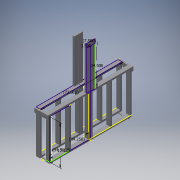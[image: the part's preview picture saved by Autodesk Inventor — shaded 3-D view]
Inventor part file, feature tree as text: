
AUTODESK INVENTOR PART (.ipt)
format: ipt  version: 2019 (Build 230136000, 136)  size: 350,720 bytes
history: native  units: in
note: dims shown in document units (in); Inventor stores cm internally (conversion verified against a paired STEP export)
features: sketch x19, extrude x8
ambient origin geometry x8: Origin, YZ Plane, XZ Plane, XY Plane, X Axis, Y Axis, Z Axis, Center Point
bodies: Solid1 (feature_tree), Solid2 (feature_tree)
feature tree (27):
  extrude  "Extrusion1"  Depth=72.0in
  extrude  "Extrusion3"  Depth=3.5in
  extrude  "Extrusion7"  Depth=1.5in
  extrude  "Extrusion8"  Depth=1.5in
  extrude  "Extrusion9"  Depth=1.5in
  extrude  "Extrusion11"  Depth=1.5in
  extrude  "Extrusion12"  Depth=1.5in
  extrude  "Extrusion13"  Depth=1.5in
  sketch  "Sketch19"  dims[d23=1.5in]
  sketch  "Sketch20"  dims[d24=3.5in]
  sketch  "Sketch21"  dims[d25=3.5in]
  sketch  "Sketch22"  dims[d26=3.5in]
  sketch  "Sketch23"  dims[d27=1.5in]
  sketch  "Sketch24"  dims[d28=1.5in]
  sketch  "Sketch25"  dims[d29=34.5in d30=0.0in]
  sketch  "Sketch26"  dims[d50=1.5in d51=0.0in]
  sketch  "Sketch27"  dims[d52=1.5in]
  sketch  "Sketch28"  dims[d53=3.5in]
  sketch  "Sketch29"  dims[d54=1.5in d55=3.5in d56=1.5in d57=3.5in d58=1.5in d59=3.5in d60=34.5in d61=0.0in d62=3.5in d63=0.0in d75=1.5in d76=1.5in d77=0.5in d78=0.0in d79=3.5in d80=1.5in d81=0.0in d82=1.5in d83=0.0in d84=34.5in d85=72.0in d87=34.5in d88=3.5in d89=7.5in d90=17.125in d91=34.25in]
  sketch  "Sketch1"  dims[d0=12.0in d1=72.0in]
  sketch  "Sketch2"  dims[d2=3.5in d3=3.5in]
  sketch  "Sketch10"  dims[d4=1.5in d5=0.0in d6=1.5in]
  sketch  "Sketch11"  dims[d8=0.5in d9=1.5in]
  sketch  "Sketch13"  dims[d10=1.5in d11=1.5in]
  sketch  "Sketch16"  dims[d17=1.5in d18=1.5in]
  sketch  "Sketch17"  dims[d19=3.5in d20=1.5in]
  sketch  "Sketch18"  dims[d21=3.5in d22=1.5in]
